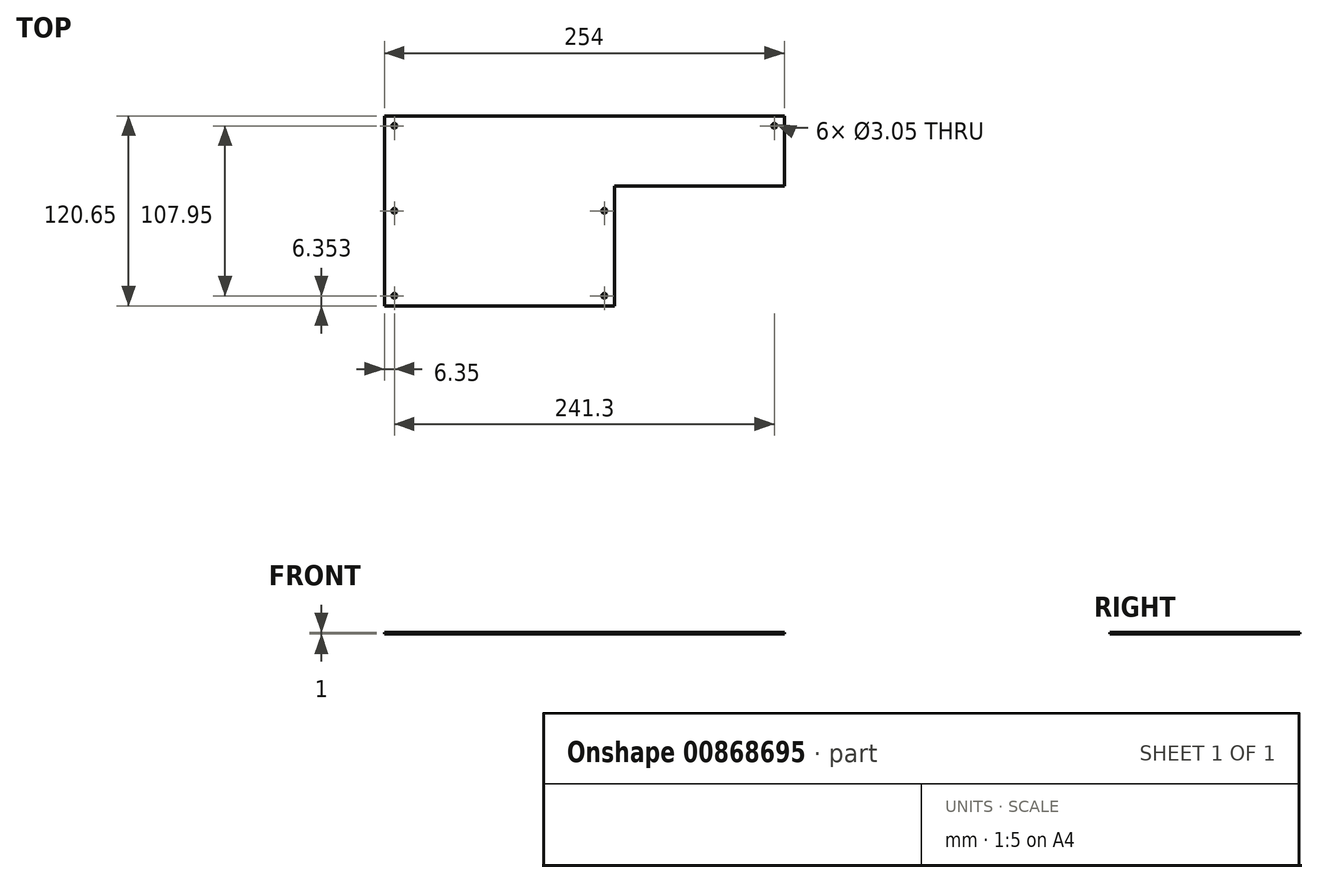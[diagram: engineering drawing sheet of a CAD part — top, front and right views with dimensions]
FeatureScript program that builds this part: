
annotation { "Feature Type Name" : "Feature", "Feature Type Description" : "" }
export const myFeature = defineFeature(function(context is Context, id is Id, definition is map)
    precondition{}
    {
        {
            var Q0;
            Q0=qCreatedBy(makeId("Top.planeOp"),FACE);
            var sketch = newSketch(context, id + "F0", { "sketchPlane" : qUnion([Q0])});
            skLineSegment(sketch, "E0", {"start": v(-127, 56.15) * mm, "end": v(127, 56.15) * mm});
            skLineSegment(sketch, "E1", {"start": v(127, 56.15) * mm, "end": v(127, 11.7) * mm});
            skLineSegment(sketch, "E2", {"start": v(127, 11.7) * mm, "end": v(19.05, 11.7) * mm});
            skLineSegment(sketch, "E3", {"start": v(19.05, 11.7) * mm, "end": v(19.05, -64.5) * mm});
            skLineSegment(sketch, "E4", {"start": v(19.05, -64.5) * mm, "end": v(-127, -64.5) * mm});
            skLineSegment(sketch, "E5", {"start": v(-127, -64.5) * mm, "end": v(-127, 11.7) * mm});
            skLineSegment(sketch, "E6", {"start": v(-127, 11.7) * mm, "end": v(-127, 11.7) * mm});
            skLineSegment(sketch, "E7", {"start": v(-127, 11.7) * mm, "end": v(-127, 56.15) * mm});
            skSolve(sketch);
        }
        {
            var Q0;
            Q0=makeQuery(id+"F0.imprint","IMPRINT",FACE,{"disambiguationData":[TD([[makeQuery(id+"F0.imprint","IMPRINT",EDGE,{"derivedFrom":sQuery(id+"F0.wireOp",EDGE,"ULd2588Q-JHcO-3Ezt-B4LH-CQlkXiQgMfxx.bottom")}),-1.0]])]});
            var Q1;
            Q1=makeQuery(id+"F0.imprint","IMPRINT",FACE,{"disambiguationData":[TD([[makeQuery(id+"F0.imprint","IMPRINT",EDGE,{"derivedFrom":sQuery(id+"F0.wireOp",EDGE,"E0")}),-1.0]])]});
            extrude(context, id + "F1", {"entities" : qUnion([Q0, Q1]), "depth" : 1 * mm, "offsetDistance" : 25.4 * mm});
        }
        {
            var Q0;
            Q0=makeQuery(id+"F1.opExtrude","CAP_FACE",FACE,{"disambiguationData":[OSD([sQuery(id+"F0.wireOp",EDGE,"E0"),sQuery(id+"F0.wireOp",EDGE,"E1"),sQuery(id+"F0.wireOp",EDGE,"E2"),sQuery(id+"F0.wireOp",EDGE,"E3"),sQuery(id+"F0.wireOp",EDGE,"E4"),sQuery(id+"F0.wireOp",EDGE,"E5"),sQuery(id+"F0.wireOp",EDGE,"E6"),sQuery(id+"F0.wireOp",EDGE,"E7")])],"isStart":false});
            var sketch = newSketch(context, id + "F2", { "sketchPlane" : qUnion([Q0])});
            skPoint(sketch, "E8", {"position": v(-120.65, 49.8) * mm});
            skPoint(sketch, "E9", {"position": v(120.65, 49.8) * mm});
            skPoint(sketch, "E10", {"position": v(-120.65, -58.15) * mm});
            skPoint(sketch, "E11", {"position": v(12.7, -58.15) * mm});
            skPoint(sketch, "E12", {"position": v(12.7, -4.17) * mm});
            skPoint(sketch, "E13", {"position": v(-120.65, -4.17) * mm});
            skSolve(sketch);
        }
        {
            var Q0;
            Q0=sQuery(id+"F2.wireOp",VERTEX,"E8");
            var Q1;
            Q1=sQuery(id+"F2.wireOp",VERTEX,"E13");
            var Q2;
            Q2=sQuery(id+"F2.wireOp",VERTEX,"66a9716a-c9b2-47ee-a24c-79c3dfbf9f7d");
            var Q3;
            Q3=sQuery(id+"F2.wireOp",VERTEX,"E10");
            var Q4;
            Q4=sQuery(id+"F2.wireOp",VERTEX,"E11");
            var Q5;
            Q5=sQuery(id+"F2.wireOp",VERTEX,"744322c6-2193-4676-96b0-13c008b3ddec");
            var Q6;
            Q6=sQuery(id+"F2.wireOp",VERTEX,"E12");
            var Q7;
            Q7=sQuery(id+"F2.wireOp",VERTEX,"E9");
            var Q8;
            Q8=makeQuery(id+"F1.opExtrude","SWEPT_BODY",BODY,{"disambiguationData":[OSD([sQuery(id+"F0.wireOp",EDGE,"E0"),sQuery(id+"F0.wireOp",EDGE,"E1"),sQuery(id+"F0.wireOp",EDGE,"E2"),sQuery(id+"F0.wireOp",EDGE,"E3"),sQuery(id+"F0.wireOp",EDGE,"E4"),sQuery(id+"F0.wireOp",EDGE,"E5"),sQuery(id+"F0.wireOp",EDGE,"E6"),sQuery(id+"F0.wireOp",EDGE,"E7")])]});
            hole(context, id + "F3", {"style" : HoleStyle.SIMPLE, "endStyle" : HoleEndStyle.BLIND, "standardTappedOrClearance" : lookupTablePath({ "fit" : "Close (ASME)", "standard" : "ANSI", "size" : "#4", "type" : "Clearance" }), "standardBlindInLast" : lookupTablePath({ "fit" : "Close", "standard" : "ANSI", "size" : "#4", "type" : "Clearance" }), "holeDiameter" : 3.05 * mm, "majorDiameter" : 6.35 * mm, "holeDepth" : 12.7 * mm, "isTappedThrough" : true, "tappedDepth" : 12.7 * mm, "tapClearance" : 3, "locations" : qUnion([Q0, Q1, Q2, Q3, Q4, Q5, Q6, Q7]), "scope" : qUnion([Q8])});
        }
    });
